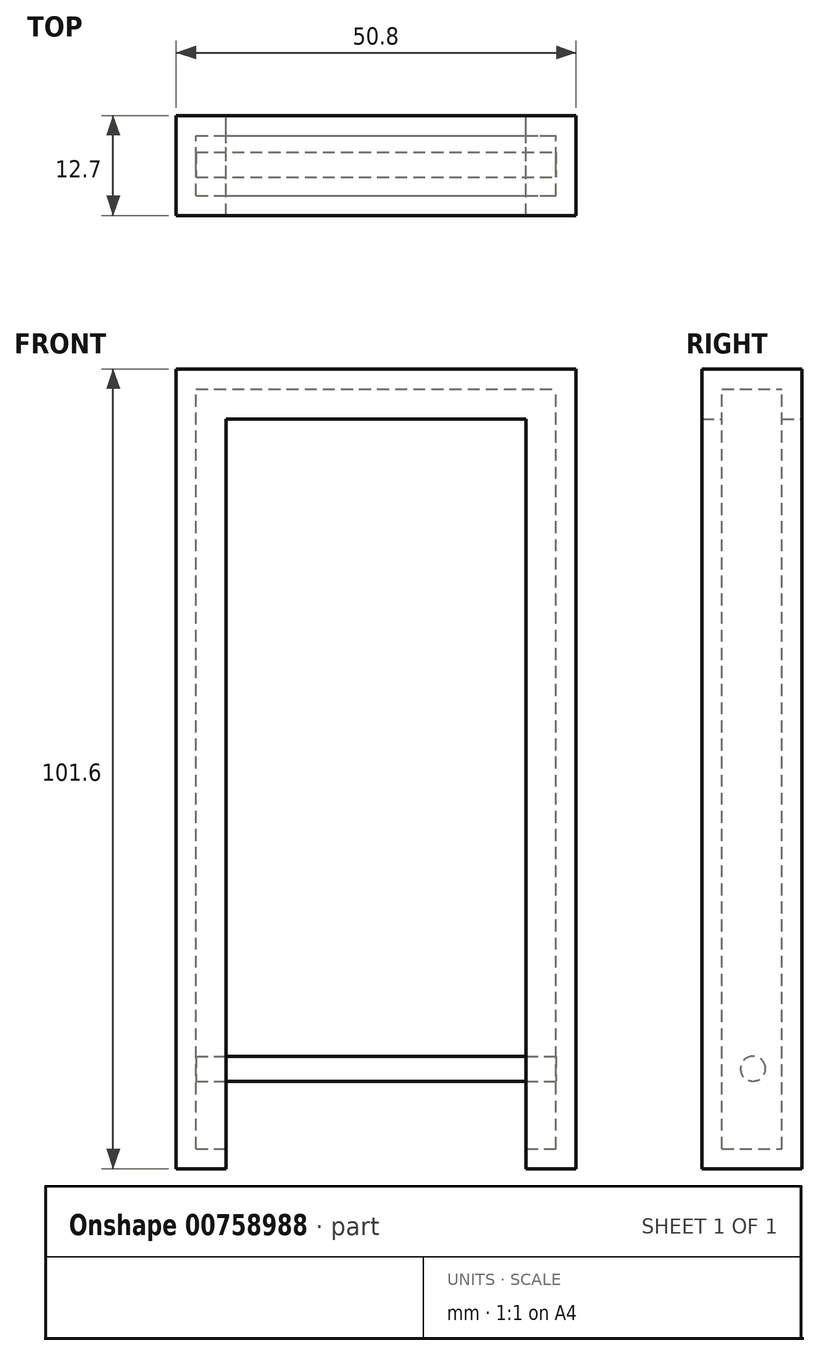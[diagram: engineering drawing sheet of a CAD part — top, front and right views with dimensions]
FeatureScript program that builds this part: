
annotation { "Feature Type Name" : "Feature", "Feature Type Description" : "" }
export const myFeature = defineFeature(function(context is Context, id is Id, definition is map)
    precondition{}
    {
        {
            var Q0;
            Q0=qCreatedBy(makeId("Front.planeOp"),FACE);
            var sketch = newSketch(context, id + "F0", { "sketchPlane" : qUnion([Q0])});
            skLineSegment(sketch, "E0.bottom", {"start": v(-105.32, -12.7) * mm, "end": v(-54.52, -12.7) * mm});
            skLineSegment(sketch, "E0.top", {"start": v(-105.32, 88.9) * mm, "end": v(-54.52, 88.9) * mm});
            skLineSegment(sketch, "E0.left", {"start": v(-105.32, -12.7) * mm, "end": v(-105.32, 88.9) * mm});
            skLineSegment(sketch, "E0.right", {"start": v(-54.52, -12.7) * mm, "end": v(-54.52, 88.9) * mm});
            skLineSegment(sketch, "E1.top", {"start": v(-98.97, 82.55) * mm, "end": v(-60.87, 82.55) * mm});
            skLineSegment(sketch, "E1.left", {"start": v(-98.97, 0) * mm, "end": v(-98.97, 82.55) * mm});
            skLineSegment(sketch, "E1.right", {"start": v(-60.87, 0) * mm, "end": v(-60.87, 82.55) * mm});
            skLineSegment(sketch, "E2", {"start": v(-98.97, 0) * mm, "end": v(-98.97, -12.7) * mm});
            skLineSegment(sketch, "E3", {"start": v(-60.87, 0) * mm, "end": v(-60.87, -12.7) * mm});
            skLineSegment(sketch, "E4", {"start": v(-60.87, -12.7) * mm, "end": v(-98.97, -12.7) * mm});
            skSolve(sketch);
        }
        {
            var Q0;
            Q0=makeQuery(id+"F0.imprint","IMPRINT",FACE,{"disambiguationData":[TD([[makeQuery(id+"F0.imprint","IMPRINT",EDGE,{"derivedFrom":sQuery(id+"F0.wireOp",EDGE,"E0.bottom")}),1.0]])]});
            extrude(context, id + "F1", {"entities" : qUnion([Q0]), "depth" : 12.7 * mm, "offsetDistance" : 25.4 * mm});
        }
        {
            var Q0;
            Q0=makeQuery(id+"F1.opExtrude","SWEPT_FACE",FACE,{"disambiguationData":[OSD([sQuery(id+"F0.wireOp",EDGE,"E1.bottom")])]});
            var Q1;
            Q1=makeQuery(id+"F1.opExtrude","SWEPT_FACE",FACE,{"disambiguationData":[OSD([sQuery(id+"F0.wireOp",EDGE,"E1.right")])]});
            var Q2;
            Q2=makeQuery(id+"F1.opExtrude","SWEPT_FACE",FACE,{"disambiguationData":[OSD([sQuery(id+"F0.wireOp",EDGE,"E1.top")])]});
            var Q3;
            Q3=makeQuery(id+"F1.opExtrude","SWEPT_FACE",FACE,{"disambiguationData":[OSD([sQuery(id+"F0.wireOp",EDGE,"E1.left")])]});
            shell(context, id + "F2", {"entities" : qUnion([Q0, Q1, Q2, Q3]), "thickness" : 2.54 * mm});
        }
        {
            var Q0;
            Q0=makeQuery(id+"F2.opShell","OFFSET_FACE",FACE,{"disambiguationData":[OSD([sQuery(id+"F0.wireOp",EDGE,"E0.right")])]});
            var sketch = newSketch(context, id + "F3", { "sketchPlane" : qUnion([Q0])});
            skCircle(sketch, "E5", {"center": v(6.23, 0) * mm, "radius": 1.59 * mm});
            skSolve(sketch);
        }
        {
            var Q0;
            Q0 = qSketchRegion(id + "F3", true);
            extrude(context, id + "F4", {"entities" : qUnion([Q0]), "operationType" : NewBodyOperationType.ADD, "depth" : 45.72 * mm, "offsetDistance" : 25.4 * mm});
        }
    });
